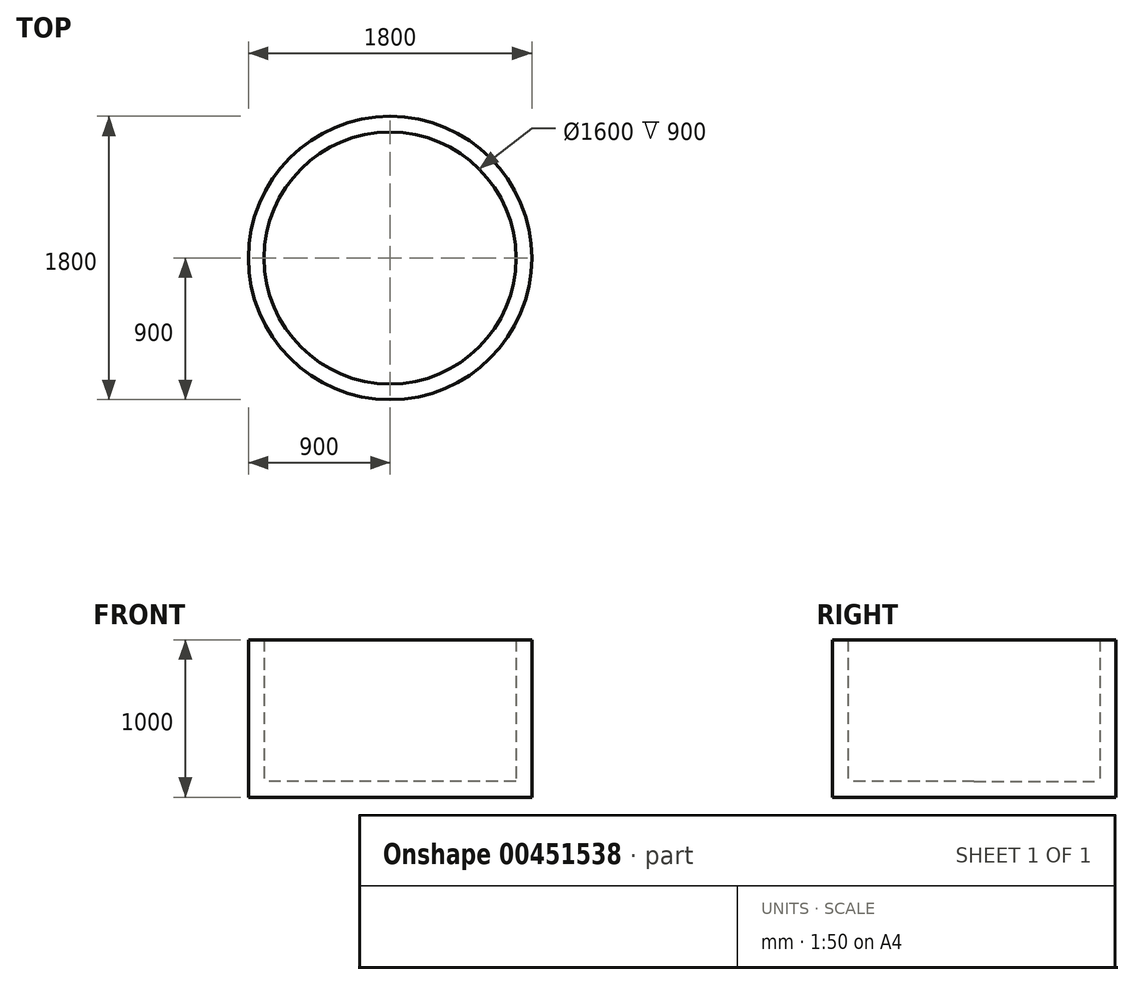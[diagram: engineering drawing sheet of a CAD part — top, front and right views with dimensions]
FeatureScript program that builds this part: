
annotation { "Feature Type Name" : "Feature", "Feature Type Description" : "" }
export const myFeature = defineFeature(function(context is Context, id is Id, definition is map)
    precondition{}
    {
        {
            var Q0;
            Q0=qCreatedBy(makeId("Top.planeOp"),FACE);
            var sketch = newSketch(context, id + "F0", { "sketchPlane" : qUnion([Q0])});
            skCircle(sketch, "E0", {"center": v(0, 0) * mm, "radius": 900 * mm});
            skSolve(sketch);
        }
        {
            var Q0;
            Q0=makeQuery(id+"F0.imprint","IMPRINT",FACE,{"disambiguationData":[TD([[makeQuery(id+"F0.imprint","IMPRINT",EDGE,{"derivedFrom":sQuery(id+"F0.wireOp",EDGE,"E0")}),1.0]])]});
            extrude(context, id + "F1", {"entities" : qUnion([Q0]), "endBound" : BoundingType.SYMMETRIC, "depth" : 100 * mm});
        }
        {
            var Q0;
            Q0=makeQuery(id+"F1.opExtrude","CAP_FACE",FACE,{"disambiguationData":[OSD([sQuery(id+"F0.wireOp",EDGE,"E0")])],"isStart":true});
            var sketch = newSketch(context, id + "F2", { "sketchPlane" : qUnion([Q0])});
            skCircle(sketch, "E1.0.0", {"center": v(0, 0) * mm, "radius": 900 * mm});
            skCircle(sketch, "E2", {"center": v(0, 0) * mm, "radius": 800 * mm});
            skSolve(sketch);
        }
        {
            var Q0;
            Q0=makeQuery(id+"F2.imprint","IMPRINT",FACE,{"disambiguationData":[TD([[makeQuery(id+"F2.imprint","IMPRINT",EDGE,{"derivedFrom":sQuery(id+"F2.wireOp",EDGE,"E1.0.0")}),-1.0]])]});
            extrude(context, id + "F3", {"entities" : qUnion([Q0]), "operationType" : NewBodyOperationType.ADD, "oppositeDirection" : true, "depth" : 1000 * mm});
        }
        {
            var Q0;
            Q0=qCreatedBy(makeId("Front.planeOp"),FACE);
            var Q1;
            Q1=makeQuery(id+"F3.boolean.opBoolean","INTERSECT",EDGE,{"derivedFrom":[makeQuery(id+"F1.opExtrude","CAP_FACE",FACE,{"disambiguationData":[OSD([sQuery(id+"F0.wireOp",EDGE,"E0")])],"isStart":false}),makeQuery(id+"F3.opExtrude","SWEPT_FACE",FACE,{"disambiguationData":[OSD([sQuery(id+"F2.wireOp",EDGE,"E2")])]})]});
            cPlane(context, id + "F5", {"entities" : qUnion([Q0, Q1]), "cplaneType" : CPlaneType.LINE_ANGLE, "offset" : 25 * mm, "angle" : 125 * degree, "oppositeDirection" : true, "width" : 150 * mm, "height" : 150 * mm});
        }
    });
